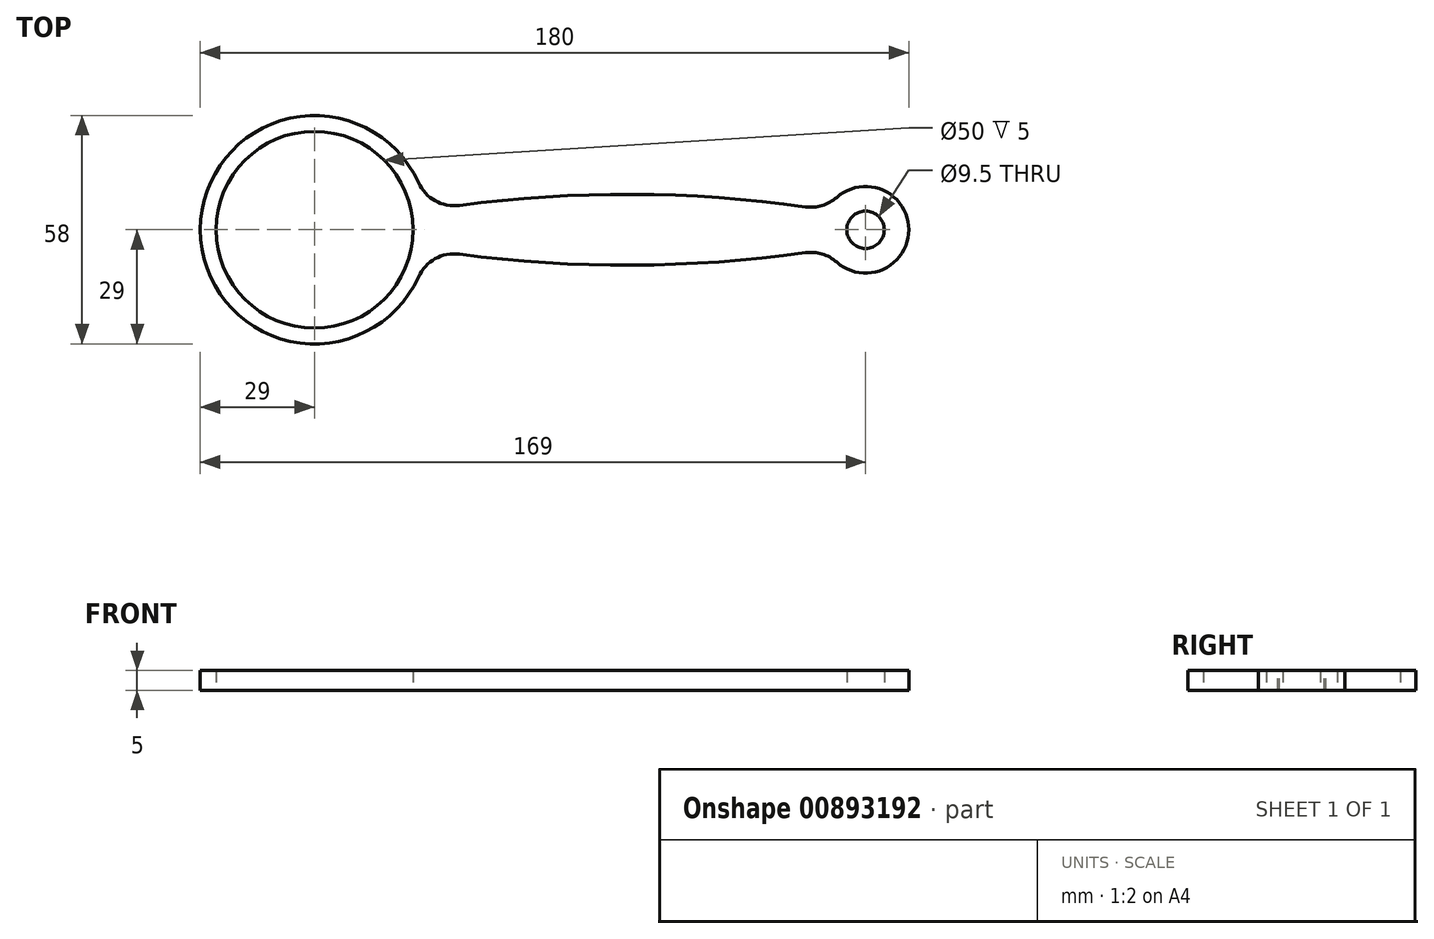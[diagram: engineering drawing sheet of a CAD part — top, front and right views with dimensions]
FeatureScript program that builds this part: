
annotation { "Feature Type Name" : "Feature", "Feature Type Description" : "" }
export const myFeature = defineFeature(function(context is Context, id is Id, definition is map)
    precondition{}
    {
        {
            var Q0;
            Q0=qCreatedBy(makeId("Top.planeOp"),FACE);
            var sketch = newSketch(context, id + "F0", { "sketchPlane" : qUnion([Q0])});
            skArc(sketch, "E0", {"start": v(28.57, 5) * mm, "mid": v(-29, 0) * mm, "end": v(28.57, -5) * mm});
            skCircle(sketch, "E1", {"center": v(0, 0) * mm, "radius": 25 * mm});
            skCircle(sketch, "E2", {"center": v(140, 0) * mm, "radius": 4.75 * mm});
            skArc(sketch, "E3", {"start": v(130.2, -5) * mm, "mid": v(151, 0) * mm, "end": v(130.2, 5) * mm});
            skArc(sketch, "E4", {"start": v(130.2, 5) * mm, "mid": v(79.38, 9) * mm, "end": v(28.57, 5) * mm});
            skArc(sketch, "E5.MirrorCS", {"start": v(130.2, -5) * mm, "mid": v(79.38, -9) * mm, "end": v(28.57, -5) * mm});
            skSolve(sketch);
        }
        {
            var Q0;
            Q0=makeQuery(id+"F0.imprint","IMPRINT",FACE,{"disambiguationData":[TD([[makeQuery(id+"F0.imprint","IMPRINT",EDGE,{"derivedFrom":sQuery(id+"F0.wireOp",EDGE,"E0")}),1.0]])]});
            extrude(context, id + "F1", {"entities" : qUnion([Q0]), "depth" : 5 * mm, "offsetDistance" : 25 * mm});
        }
        {
            var Q0;
            Q0=makeQuery(id+"F1.opExtrude","SWEPT_EDGE",EDGE,{"disambiguationData":[OSD([sQuery(id+"F0.wireOp",EDGE,"E0"),sQuery(id+"F0.wireOp",EDGE,"E5.MirrorCS")])]});
            var Q1;
            Q1=makeQuery(id+"F1.opExtrude","SWEPT_EDGE",EDGE,{"disambiguationData":[OSD([sQuery(id+"F0.wireOp",EDGE,"E0"),sQuery(id+"F0.wireOp",EDGE,"E4")])]});
            var Q2;
            Q2=makeQuery(id+"F1.opExtrude","SWEPT_EDGE",EDGE,{"disambiguationData":[OSD([sQuery(id+"F0.wireOp",EDGE,"E3"),sQuery(id+"F0.wireOp",EDGE,"E4")])]});
            var Q3;
            Q3=makeQuery(id+"F1.opExtrude","SWEPT_EDGE",EDGE,{"disambiguationData":[OSD([sQuery(id+"F0.wireOp",EDGE,"E3"),sQuery(id+"F0.wireOp",EDGE,"E5.MirrorCS")])]});
            fillet(context, id + "F2", {"entities" : qUnion([Q0, Q1, Q2, Q3]), "radius" : 10 * mm, "tangentPropagation" : true, "allowEdgeOverflow" : false});
        }
    });
